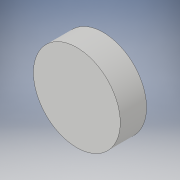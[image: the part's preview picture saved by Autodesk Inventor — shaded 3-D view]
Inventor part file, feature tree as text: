
AUTODESK INVENTOR PART (.ipt)
format: ipt  version: 2019 (Build 230136000, 136)  size: 91,136 bytes
history: native  units: mm
features: other x1, extrude x1, sketch x1
ambient origin geometry x8: Origin, YZ Plane, XZ Plane, XY Plane, X Axis, Y Axis, Z Axis, Center Point
bodies: Body1 (feature_tree)
feature tree (3):
  other  "實體1"
  extrude  "擠出1"  Depth=33.0mm
  sketch  "草圖1"
